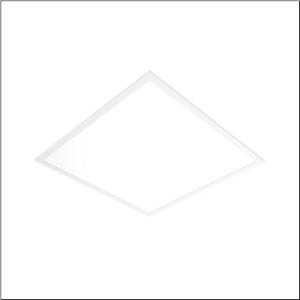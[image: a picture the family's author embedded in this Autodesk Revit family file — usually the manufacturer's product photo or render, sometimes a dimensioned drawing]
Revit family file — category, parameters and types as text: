
# Revit family: apollon_r__41_51mh11wd2n43_c469
name_source: partatom
category: Lighting Fixtures
units: mm (PartAtom-declared; Revit-internal decimal feet)

## family parameters
Cut with Voids When Loaded = No
Host = Face
Light Source = No
Part Type = Normal
Room Calculation Point = No
Round Connector Dimension = Use Diameter
Shared = No

## types (1)
- --- (1 x LED, 3450 lm, 28.5 W, 6500K)
    Apparent Load = 29 VA
    CIE Flux Codes = 61 87 97 100 100
    Color Rendering = 80
    Color Temperature = 6500K
    Default Elevation = 1800 mm
    Description = Apollon® 41, office luminaire, primary optical cover: prismatic diffuser, of PS, light emission: direct distribution, primary light characteristic: symmetric, installation type: lay-in mounting, LED, rated luminous flux: 3.500lm, luminous efficacy: 123lm/W, light colour: 840/865, colour temperature: 4000/6500K, with terminal, 5-pole, mains connection: 220..240V, AC/DC, 0/50..60Hz, housing, of aluminium section, traffic white (RAL 9016), module: M625, length: 620mm, width: 620mm, height: 28mm, housing upper side, of sheet steel, protection rating (complete): IP20, protection rating (lamp compartment, on room side): IP40, insulation class (complete): insulation class II (safety insulation), certification: CE, ENEC, permissible operating ambient temperature: -25..+40°C, packaging unit: 1 piece
    Height = 0 mm  [stored 0 ft]
    Lamp = 1 x LED
    Lamp Light Flux = 3450 lm
    Lamp Power = 28.5 W
    Lamp count = 1
    Length = 620 mm
    Luminous efficacy = 121 lm/W
    Manufacturer = Siteco
    ModVariant = No
    Model = 51MH11WD2N43
    Mounting Place = Ceiling
    Mounting Type = Recessed
    Number of Poles = 1
    OnlyDefault = Yes
    Power Factor = 1
    Product Name = Apollon® 41
    Product group = office luminaire | ceiling recessed
    ProductGroupID = 401
    Protection Class = Protection class II
    Protection Degree = IP 20
    RLX_Detail_Level = 1
    RLX_Emergency_Light_Flux = 0 lm
    RLX_Emergency_Type = 0
    RLX_Emergency_Type_DB = No
    RlxData = <blob elided: 12401 chars, md5=11d95a7c>
    Socket = socket
    Standby Power = 0 W
    System Light Flux = 3450 lm
    System Power = 29 W
    Type Comments = individual setting
    Type Image = l_1291024.jpg
    URL = http://relux.com
    VarID = @adj_008953
    Voltage = 0 V
    Weight = 0.00 kg
    Width = 620 mm

note: [stored X ft] marks values corroborated as IEEE doubles in the binary element streams (Revit-internal decimal feet)

## geometry (parser evidence)
native form markers: Sweep x8
no freeform markers — native parametric forms only
